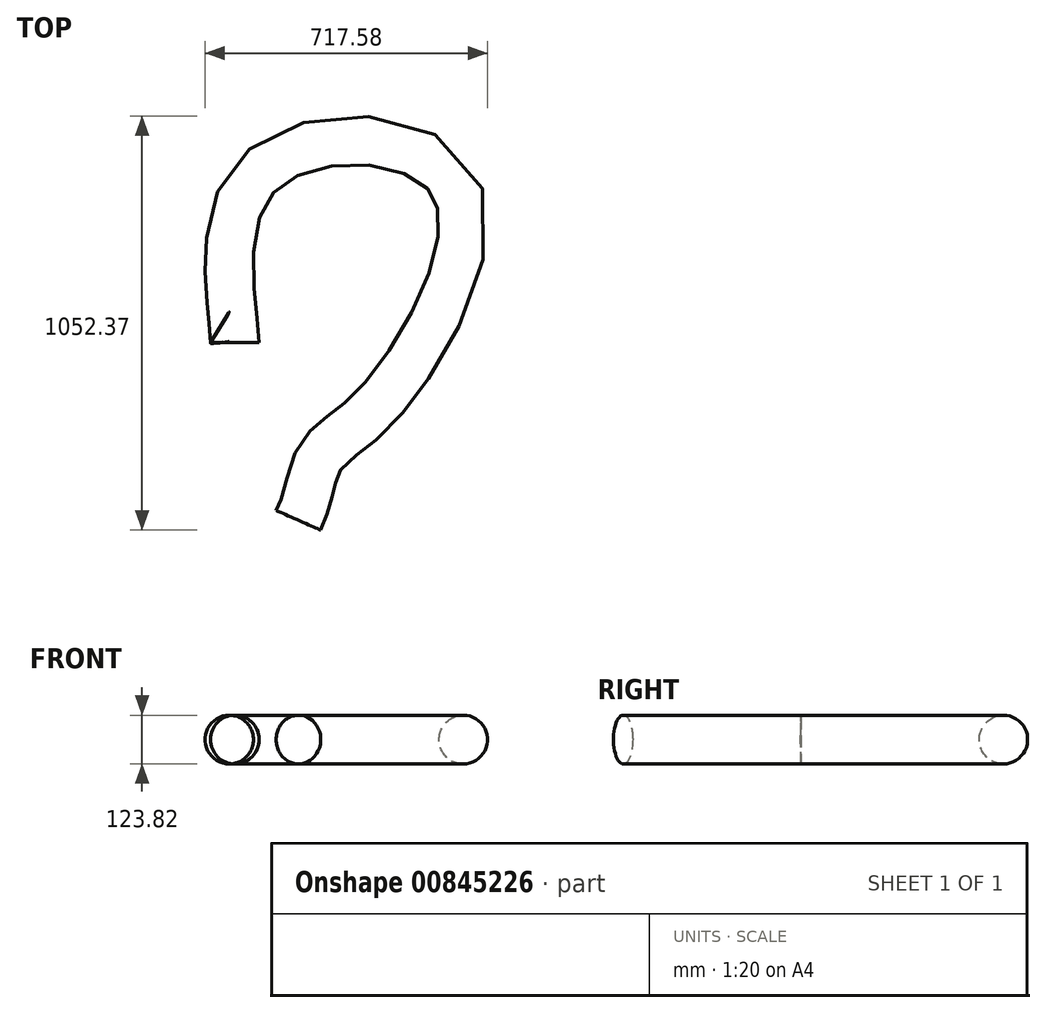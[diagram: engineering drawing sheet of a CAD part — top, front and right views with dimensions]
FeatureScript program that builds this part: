
annotation { "Feature Type Name" : "Feature", "Feature Type Description" : "" }
export const myFeature = defineFeature(function(context is Context, id is Id, definition is map)
    precondition{}
    {
        {
            var Q0;
            Q0=qCreatedBy(makeId("Front.planeOp"),FACE);
            var sketch = newSketch(context, id + "F0", { "sketchPlane" : qUnion([Q0])});
            skCircle(sketch, "E0", {"center": v(0, 0) * mm, "radius": 61.91 * mm});
            skSolve(sketch);
        }
        {
            var Q0;
            Q0=qCreatedBy(makeId("Top.planeOp"),FACE);
            var sketch = newSketch(context, id + "F1", { "sketchPlane" : qUnion([Q0])});
            skFitSpline(sketch, "E1", {"points": [v(0, 0) * mm, v(44.21, 412.8) * mm, v(554.13, 408) * mm, v(352.06, -169.13) * mm, v(215.2, -293.83) * mm, v(161.78, -451.28) * mm], "startDerivative": vector(69, 553.93) * mm, "endDerivative": vector(-466.59, -773.53) * mm});
            skSolve(sketch);
        }
        {
            var Q0;
            Q0=makeQuery(id+"F0.imprint","IMPRINT",FACE,{"disambiguationData":[TD([[makeQuery(id+"F0.imprint","IMPRINT",EDGE,{"derivedFrom":sQuery(id+"F0.wireOp",EDGE,"E0")}),1.0]])]});
            var Q1;
            Q1=sQuery(id+"F0.wireOp",EDGE,"E0");
            var Q2;
            Q2=sQuery(id+"F1.wireOp",EDGE,"E1");
            sweep(context, id + "F2", {"bodyType" : ToolBodyType.SURFACE, "profiles" : qUnion([Q0]), "surfaceProfiles" : qUnion([Q1]), "path" : qUnion([Q2])});
        }
    });
